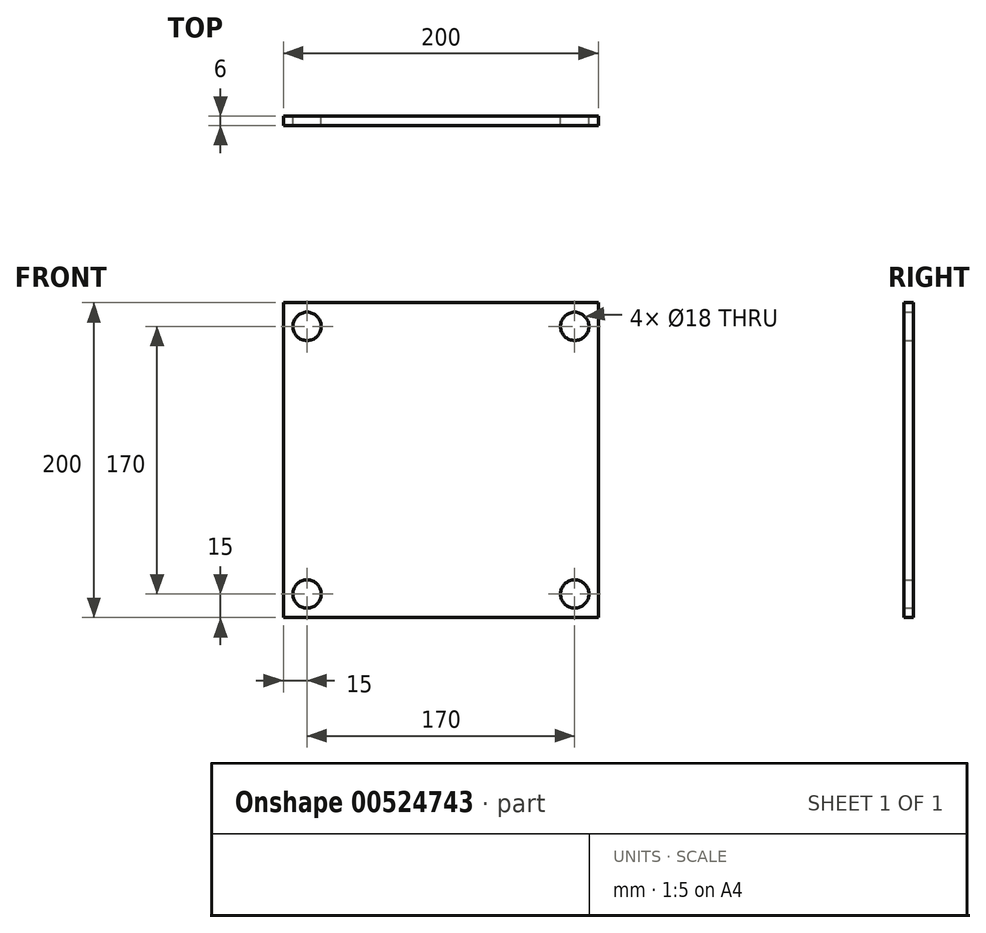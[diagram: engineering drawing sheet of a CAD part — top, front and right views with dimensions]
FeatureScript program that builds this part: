
annotation { "Feature Type Name" : "Feature", "Feature Type Description" : "" }
export const myFeature = defineFeature(function(context is Context, id is Id, definition is map)
    precondition{}
    {
        {
            var Q0;
            Q0=qCreatedBy(makeId("Front.planeOp"),FACE);
            var sketch = newSketch(context, id + "F0", { "sketchPlane" : qUnion([Q0])});
            skLineSegment(sketch, "E0.bottom", {"start": v(0, 0) * mm, "end": v(200, 0) * mm});
            skLineSegment(sketch, "E0.top", {"start": v(0, 200) * mm, "end": v(200, 200) * mm});
            skLineSegment(sketch, "E0.left", {"start": v(0, 0) * mm, "end": v(0, 200) * mm});
            skLineSegment(sketch, "E0.right", {"start": v(200, 0) * mm, "end": v(200, 200) * mm});
            skCircle(sketch, "E1", {"center": v(15, 185) * mm, "radius": 9 * mm});
            skCircle(sketch, "E2", {"center": v(185, 185) * mm, "radius": 9 * mm});
            skCircle(sketch, "E3", {"center": v(185, 15) * mm, "radius": 9 * mm});
            skCircle(sketch, "E4", {"center": v(15, 15) * mm, "radius": 9 * mm});
            skSolve(sketch);
        }
        {
            var Q0;
            Q0=makeQuery(id+"F0.imprint","IMPRINT",FACE,{"disambiguationData":[TD([[makeQuery(id+"F0.imprint","IMPRINT",EDGE,{"derivedFrom":sQuery(id+"F0.wireOp",EDGE,"E0.bottom")}),1.0]])]});
            extrude(context, id + "F1", {"entities" : qUnion([Q0]), "depth" : 6 * mm, "offsetDistance" : 25 * mm});
        }
    });
